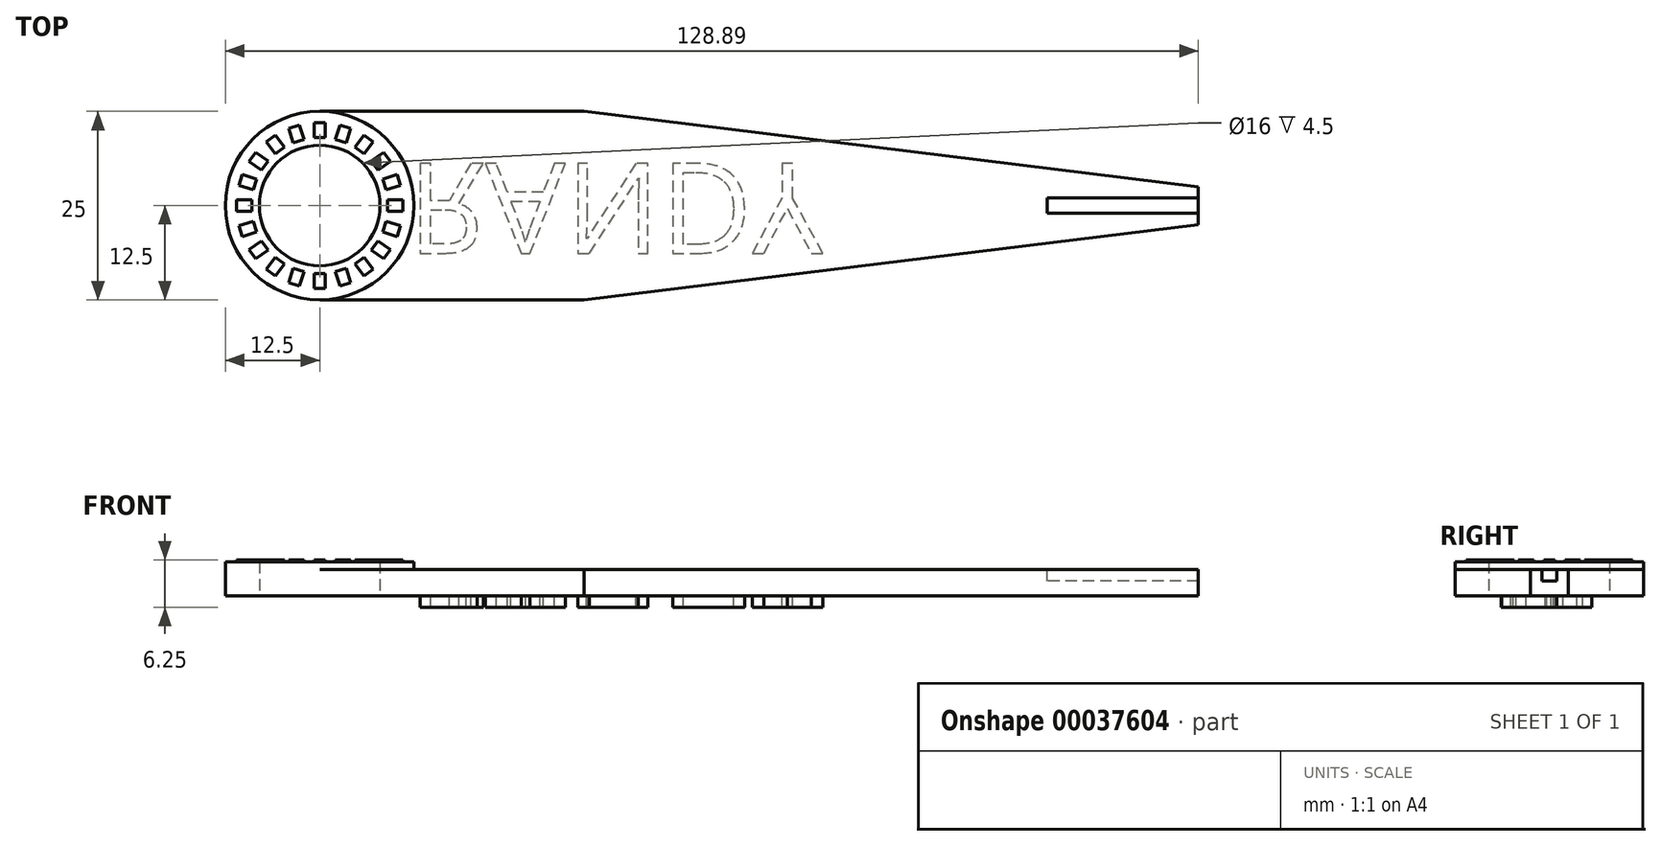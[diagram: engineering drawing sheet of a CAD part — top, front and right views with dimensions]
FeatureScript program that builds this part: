
annotation { "Feature Type Name" : "Feature", "Feature Type Description" : "" }
export const myFeature = defineFeature(function(context is Context, id is Id, definition is map)
    precondition{}
    {
        {
            var Q0;
            Q0=qCreatedBy(makeId("Top.planeOp"),FACE);
            var sketch = newSketch(context, id + "F0", { "sketchPlane" : qUnion([Q0])});
            skCircle(sketch, "E0", {"center": v(0, 0) * mm, "radius": 8 * mm});
            skCircle(sketch, "E1", {"center": v(0, 0) * mm, "radius": 12.5 * mm});
            skLineSegment(sketch, "E2", {"start": v(0, 12.5) * mm, "end": v(35, 12.5) * mm});
            skPoint(sketch, "E3", {"position": v(0, 12.5) * mm});
            skPoint(sketch, "E4", {"position": v(0, -12.5) * mm});
            skLineSegment(sketch, "E5", {"start": v(0, -12.5) * mm, "end": v(35, -12.5) * mm});
            skLineSegment(sketch, "E6", {"start": v(35, 12.5) * mm, "end": v(72.12, 12.5) * mm, "construction": true});
            skLineSegment(sketch, "E7", {"start": v(35, 12.5) * mm, "end": v(116.39, 2.5) * mm});
            skLineSegment(sketch, "E8.MirrorCS", {"start": v(35, -12.5) * mm, "end": v(116.39, -2.5) * mm});
            skLineSegment(sketch, "E9", {"start": v(116.39, 2.5) * mm, "end": v(116.39, -2.5) * mm});
            skSolve(sketch);
        }
        {
            var Q0;
            Q0 = qSketchRegion(id + "F0", true);
            extrude(context, id + "F1", {"entities" : qUnion([Q0]), "depth" : 3.5 * mm});
        }
        {
            var Q0;
            Q0=makeQuery(id+"F1.opExtrude","CAP_FACE",FACE,{"disambiguationData":[OSD([sQuery(id+"F0.wireOp",EDGE,"E0"),sQuery(id+"F0.wireOp",EDGE,"E1"),sQuery(id+"F0.wireOp",EDGE,"E2"),sQuery(id+"F0.wireOp",EDGE,"E5"),sQuery(id+"F0.wireOp",EDGE,"E7"),sQuery(id+"F0.wireOp",EDGE,"E8.MirrorCS"),sQuery(id+"F0.wireOp",EDGE,"E9")])],"isStart":false});
            var sketch = newSketch(context, id + "F2", { "sketchPlane" : qUnion([Q0])});
            skCircle(sketch, "E10", {"center": v(0, 0) * mm, "radius": 12.5 * mm});
            skCircle(sketch, "E11", {"center": v(0, 0) * mm, "radius": 8 * mm});
            skSolve(sketch);
        }
        {
            var Q0;
            Q0 = qSketchRegion(id + "F2", true);
            extrude(context, id + "F3", {"entities" : qUnion([Q0]), "operationType" : NewBodyOperationType.ADD, "depth" : 1 * mm});
        }
        {
            var Q0;
            Q0=makeQuery(id+"F3.opExtrude","CAP_FACE",FACE,{"disambiguationData":[OSD([sQuery(id+"F2.wireOp",EDGE,"E10"),sQuery(id+"F2.wireOp",EDGE,"E11")])],"isStart":false});
            var sketch = newSketch(context, id + "F4", { "sketchPlane" : qUnion([Q0])});
            skLineSegment(sketch, "E12.bottom", {"start": v(-0.75, 11) * mm, "end": v(0.75, 11) * mm});
            skLineSegment(sketch, "E12.top", {"start": v(-0.75, 9) * mm, "end": v(0.75, 9) * mm});
            skLineSegment(sketch, "E12.left", {"start": v(-0.75, 11) * mm, "end": v(-0.75, 9) * mm});
            skLineSegment(sketch, "E12.right", {"start": v(0.75, 11) * mm, "end": v(0.75, 9) * mm});
            skPoint(sketch, "E13", {"position": v(0, 8) * mm});
            skLineSegment(sketch, "E14.1.0", {"start": v(-4.11, 10.23) * mm, "end": v(-2.69, 10.7) * mm});
            skLineSegment(sketch, "E14.1.1", {"start": v(-2.69, 10.7) * mm, "end": v(-2.07, 8.8) * mm});
            skLineSegment(sketch, "E14.1.2", {"start": v(-3.5, 8.33) * mm, "end": v(-2.07, 8.8) * mm});
            skLineSegment(sketch, "E14.1.3", {"start": v(-4.11, 10.23) * mm, "end": v(-3.5, 8.33) * mm});
            skLineSegment(sketch, "E14.2.0", {"start": v(-7.07, 8.46) * mm, "end": v(-5.86, 9.34) * mm});
            skLineSegment(sketch, "E14.2.1", {"start": v(-5.86, 9.34) * mm, "end": v(-4.68, 7.72) * mm});
            skLineSegment(sketch, "E14.2.2", {"start": v(-5.9, 6.84) * mm, "end": v(-4.68, 7.72) * mm});
            skLineSegment(sketch, "E14.2.3", {"start": v(-7.07, 8.46) * mm, "end": v(-5.9, 6.84) * mm});
            skLineSegment(sketch, "E14.3.0", {"start": v(-9.34, 5.86) * mm, "end": v(-8.46, 7.07) * mm});
            skLineSegment(sketch, "E14.3.1", {"start": v(-8.46, 7.07) * mm, "end": v(-6.84, 5.9) * mm});
            skLineSegment(sketch, "E14.3.2", {"start": v(-7.72, 4.68) * mm, "end": v(-6.84, 5.9) * mm});
            skLineSegment(sketch, "E14.3.3", {"start": v(-9.34, 5.86) * mm, "end": v(-7.72, 4.68) * mm});
            skLineSegment(sketch, "E14.4.0", {"start": v(-10.7, 2.69) * mm, "end": v(-10.23, 4.11) * mm});
            skLineSegment(sketch, "E14.4.1", {"start": v(-10.23, 4.11) * mm, "end": v(-8.33, 3.5) * mm});
            skLineSegment(sketch, "E14.4.2", {"start": v(-8.8, 2.07) * mm, "end": v(-8.33, 3.5) * mm});
            skLineSegment(sketch, "E14.4.3", {"start": v(-10.7, 2.69) * mm, "end": v(-8.8, 2.07) * mm});
            skLineSegment(sketch, "E14.5.0", {"start": v(-11, -0.75) * mm, "end": v(-11, 0.75) * mm});
            skLineSegment(sketch, "E14.5.1", {"start": v(-11, 0.75) * mm, "end": v(-9, 0.75) * mm});
            skLineSegment(sketch, "E14.5.2", {"start": v(-9, -0.75) * mm, "end": v(-9, 0.75) * mm});
            skLineSegment(sketch, "E14.5.3", {"start": v(-11, -0.75) * mm, "end": v(-9, -0.75) * mm});
            skLineSegment(sketch, "E14.6.0", {"start": v(-10.23, -4.11) * mm, "end": v(-10.7, -2.69) * mm});
            skLineSegment(sketch, "E14.6.1", {"start": v(-10.7, -2.69) * mm, "end": v(-8.8, -2.07) * mm});
            skLineSegment(sketch, "E14.6.2", {"start": v(-8.33, -3.5) * mm, "end": v(-8.8, -2.07) * mm});
            skLineSegment(sketch, "E14.6.3", {"start": v(-10.23, -4.11) * mm, "end": v(-8.33, -3.5) * mm});
            skLineSegment(sketch, "E14.7.0", {"start": v(-8.46, -7.07) * mm, "end": v(-9.34, -5.86) * mm});
            skLineSegment(sketch, "E14.7.1", {"start": v(-9.34, -5.86) * mm, "end": v(-7.72, -4.68) * mm});
            skLineSegment(sketch, "E14.7.2", {"start": v(-6.84, -5.9) * mm, "end": v(-7.72, -4.68) * mm});
            skLineSegment(sketch, "E14.7.3", {"start": v(-8.46, -7.07) * mm, "end": v(-6.84, -5.9) * mm});
            skLineSegment(sketch, "E14.8.0", {"start": v(-5.86, -9.34) * mm, "end": v(-7.07, -8.46) * mm});
            skLineSegment(sketch, "E14.8.1", {"start": v(-7.07, -8.46) * mm, "end": v(-5.9, -6.84) * mm});
            skLineSegment(sketch, "E14.8.2", {"start": v(-4.68, -7.72) * mm, "end": v(-5.9, -6.84) * mm});
            skLineSegment(sketch, "E14.8.3", {"start": v(-5.86, -9.34) * mm, "end": v(-4.68, -7.72) * mm});
            skLineSegment(sketch, "E14.9.0", {"start": v(-2.69, -10.7) * mm, "end": v(-4.11, -10.23) * mm});
            skLineSegment(sketch, "E14.9.1", {"start": v(-4.11, -10.23) * mm, "end": v(-3.5, -8.33) * mm});
            skLineSegment(sketch, "E14.9.2", {"start": v(-2.07, -8.8) * mm, "end": v(-3.5, -8.33) * mm});
            skLineSegment(sketch, "E14.9.3", {"start": v(-2.69, -10.7) * mm, "end": v(-2.07, -8.8) * mm});
            skLineSegment(sketch, "E14.10.0", {"start": v(0.75, -11) * mm, "end": v(-0.75, -11) * mm});
            skLineSegment(sketch, "E14.10.1", {"start": v(-0.75, -11) * mm, "end": v(-0.75, -9) * mm});
            skLineSegment(sketch, "E14.10.2", {"start": v(0.75, -9) * mm, "end": v(-0.75, -9) * mm});
            skLineSegment(sketch, "E14.10.3", {"start": v(0.75, -11) * mm, "end": v(0.75, -9) * mm});
            skLineSegment(sketch, "E14.11.0", {"start": v(4.11, -10.23) * mm, "end": v(2.69, -10.7) * mm});
            skLineSegment(sketch, "E14.11.1", {"start": v(2.69, -10.7) * mm, "end": v(2.07, -8.8) * mm});
            skLineSegment(sketch, "E14.11.2", {"start": v(3.5, -8.33) * mm, "end": v(2.07, -8.8) * mm});
            skLineSegment(sketch, "E14.11.3", {"start": v(4.11, -10.23) * mm, "end": v(3.5, -8.33) * mm});
            skLineSegment(sketch, "E14.12.0", {"start": v(7.07, -8.46) * mm, "end": v(5.86, -9.34) * mm});
            skLineSegment(sketch, "E14.12.1", {"start": v(5.86, -9.34) * mm, "end": v(4.68, -7.72) * mm});
            skLineSegment(sketch, "E14.12.2", {"start": v(5.9, -6.84) * mm, "end": v(4.68, -7.72) * mm});
            skLineSegment(sketch, "E14.12.3", {"start": v(7.07, -8.46) * mm, "end": v(5.9, -6.84) * mm});
            skLineSegment(sketch, "E14.13.0", {"start": v(9.34, -5.86) * mm, "end": v(8.46, -7.07) * mm});
            skLineSegment(sketch, "E14.13.1", {"start": v(8.46, -7.07) * mm, "end": v(6.84, -5.9) * mm});
            skLineSegment(sketch, "E14.13.2", {"start": v(7.72, -4.68) * mm, "end": v(6.84, -5.9) * mm});
            skLineSegment(sketch, "E14.13.3", {"start": v(9.34, -5.86) * mm, "end": v(7.72, -4.68) * mm});
            skLineSegment(sketch, "E14.14.0", {"start": v(10.7, -2.69) * mm, "end": v(10.23, -4.11) * mm});
            skLineSegment(sketch, "E14.14.1", {"start": v(10.23, -4.11) * mm, "end": v(8.33, -3.5) * mm});
            skLineSegment(sketch, "E14.14.2", {"start": v(8.8, -2.07) * mm, "end": v(8.33, -3.5) * mm});
            skLineSegment(sketch, "E14.14.3", {"start": v(10.7, -2.69) * mm, "end": v(8.8, -2.07) * mm});
            skLineSegment(sketch, "E14.15.0", {"start": v(11, 0.75) * mm, "end": v(11, -0.75) * mm});
            skLineSegment(sketch, "E14.15.1", {"start": v(11, -0.75) * mm, "end": v(9, -0.75) * mm});
            skLineSegment(sketch, "E14.15.2", {"start": v(9, 0.75) * mm, "end": v(9, -0.75) * mm});
            skLineSegment(sketch, "E14.15.3", {"start": v(11, 0.75) * mm, "end": v(9, 0.75) * mm});
            skLineSegment(sketch, "E14.16.0", {"start": v(10.23, 4.11) * mm, "end": v(10.7, 2.69) * mm});
            skLineSegment(sketch, "E14.16.1", {"start": v(10.7, 2.69) * mm, "end": v(8.8, 2.07) * mm});
            skLineSegment(sketch, "E14.16.2", {"start": v(8.33, 3.5) * mm, "end": v(8.8, 2.07) * mm});
            skLineSegment(sketch, "E14.16.3", {"start": v(10.23, 4.11) * mm, "end": v(8.33, 3.5) * mm});
            skLineSegment(sketch, "E14.17.0", {"start": v(8.46, 7.07) * mm, "end": v(9.34, 5.86) * mm});
            skLineSegment(sketch, "E14.17.1", {"start": v(9.34, 5.86) * mm, "end": v(7.72, 4.68) * mm});
            skLineSegment(sketch, "E14.17.2", {"start": v(6.84, 5.9) * mm, "end": v(7.72, 4.68) * mm});
            skLineSegment(sketch, "E14.17.3", {"start": v(8.46, 7.07) * mm, "end": v(6.84, 5.9) * mm});
            skLineSegment(sketch, "E14.18.0", {"start": v(5.86, 9.34) * mm, "end": v(7.07, 8.46) * mm});
            skLineSegment(sketch, "E14.18.1", {"start": v(7.07, 8.46) * mm, "end": v(5.9, 6.84) * mm});
            skLineSegment(sketch, "E14.18.2", {"start": v(4.68, 7.72) * mm, "end": v(5.9, 6.84) * mm});
            skLineSegment(sketch, "E14.18.3", {"start": v(5.86, 9.34) * mm, "end": v(4.68, 7.72) * mm});
            skLineSegment(sketch, "E14.19.0", {"start": v(2.69, 10.7) * mm, "end": v(4.11, 10.23) * mm});
            skLineSegment(sketch, "E14.19.1", {"start": v(4.11, 10.23) * mm, "end": v(3.5, 8.33) * mm});
            skLineSegment(sketch, "E14.19.2", {"start": v(2.07, 8.8) * mm, "end": v(3.5, 8.33) * mm});
            skLineSegment(sketch, "E14.19.3", {"start": v(2.69, 10.7) * mm, "end": v(2.07, 8.8) * mm});
            skPoint(sketch, "E14.center", {"position": v(0, 0) * mm});
            skSolve(sketch);
        }
        {
            var Q0;
            Q0 = qSketchRegion(id + "F4", true);
            extrude(context, id + "F5", {"entities" : qUnion([Q0]), "operationType" : NewBodyOperationType.ADD, "depth" : .25 * mm});
        }
        {
            var Q0;
            Q0=makeQuery(id+"F1.opExtrude","CAP_FACE",FACE,{"disambiguationData":[OSD([sQuery(id+"F0.wireOp",EDGE,"E0"),sQuery(id+"F0.wireOp",EDGE,"E1"),sQuery(id+"F0.wireOp",EDGE,"E2"),sQuery(id+"F0.wireOp",EDGE,"E5"),sQuery(id+"F0.wireOp",EDGE,"E7"),sQuery(id+"F0.wireOp",EDGE,"E8.MirrorCS"),sQuery(id+"F0.wireOp",EDGE,"E9")])],"isStart":false});
            var sketch = newSketch(context, id + "F6", { "sketchPlane" : qUnion([Q0])});
            skLineSegment(sketch, "E15.bottom", {"start": v(116.39, 1) * mm, "end": v(96.39, 1) * mm});
            skLineSegment(sketch, "E15.top", {"start": v(116.39, -1) * mm, "end": v(96.39, -1) * mm});
            skLineSegment(sketch, "E15.left", {"start": v(116.39, 1) * mm, "end": v(116.39, -1) * mm});
            skLineSegment(sketch, "E15.right", {"start": v(96.39, 1) * mm, "end": v(96.39, -1) * mm});
            skSolve(sketch);
        }
        {
            var Q0;
            Q0 = qSketchRegion(id + "F6", true);
            extrude(context, id + "F7", {"entities" : qUnion([Q0]), "operationType" : NewBodyOperationType.REMOVE, "oppositeDirection" : true, "depth" : 1.5 * mm});
        }
        {
            var Q0;
            Q0=makeQuery(id+"F1.opExtrude","CAP_FACE",FACE,{"disambiguationData":[OSD([sQuery(id+"F0.wireOp",EDGE,"E0"),sQuery(id+"F0.wireOp",EDGE,"E1"),sQuery(id+"F0.wireOp",EDGE,"E2"),sQuery(id+"F0.wireOp",EDGE,"E5"),sQuery(id+"F0.wireOp",EDGE,"E7"),sQuery(id+"F0.wireOp",EDGE,"E8.MirrorCS"),sQuery(id+"F0.wireOp",EDGE,"E9")])],"isStart":true});
            var sketch = newSketch(context, id + "F8", { "sketchPlane" : qUnion([Q0])});
            skText(sketch, "E16", { "text": "RANDY", "fontName": "OpenSans-Regular.ttf"});
            const initialGuessF8  = {"E16": [0.01165, -0.0056, 1, 0, 0.01202]};
            skSetInitialGuess(sketch, initialGuessF8);
            skSolve(sketch);
        }
        {
            var Q0;
            Q0 = qSketchRegion(id + "F8", true);
            extrude(context, id + "F9", {"entities" : qUnion([Q0]), "operationType" : NewBodyOperationType.ADD, "depth" : 1.5 * mm});
        }
    });
